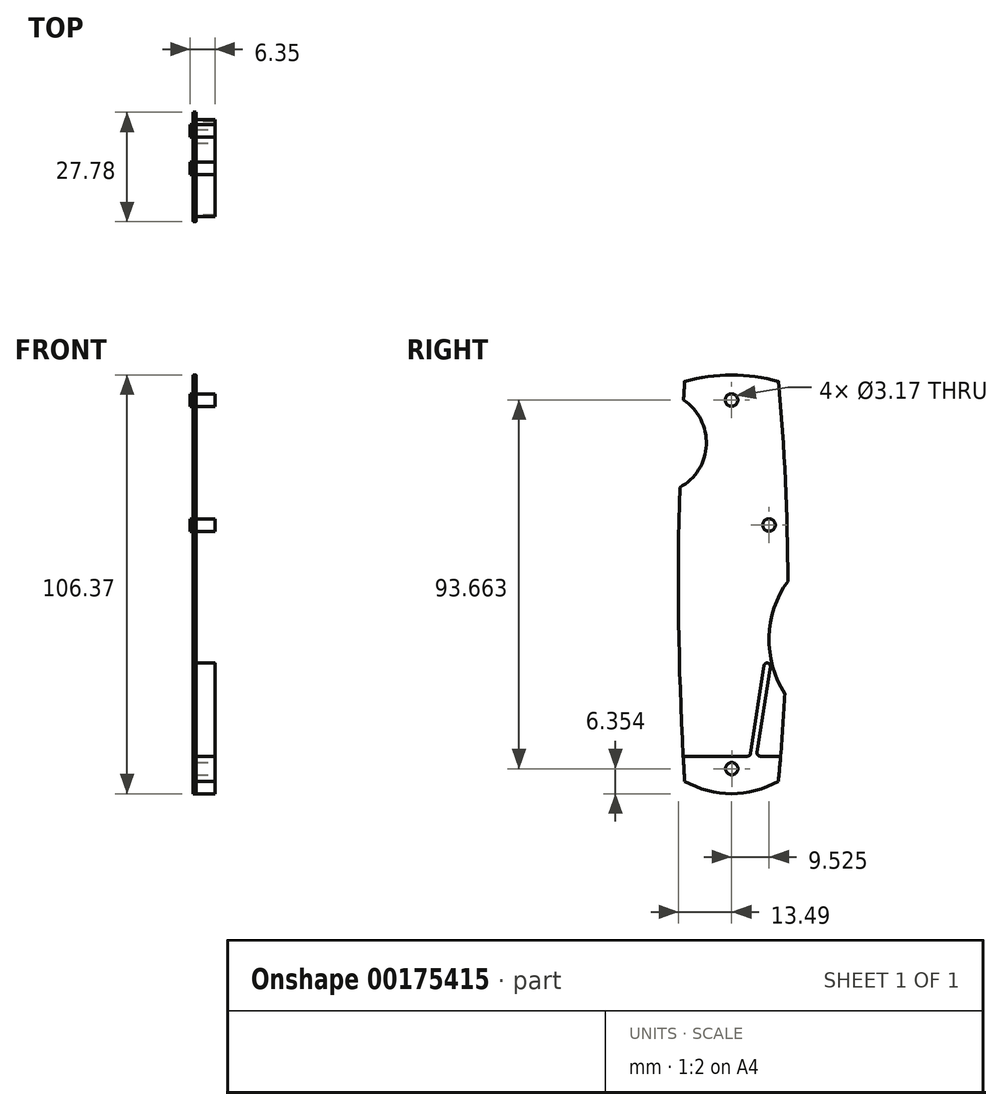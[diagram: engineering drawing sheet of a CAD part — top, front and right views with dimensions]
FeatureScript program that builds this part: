
annotation { "Feature Type Name" : "Feature", "Feature Type Description" : "" }
export const myFeature = defineFeature(function(context is Context, id is Id, definition is map)
    precondition{}
    {
        {
            var Q0;
            Q0=qCreatedBy(makeId("Right.planeOp"),FACE);
            var sketch = newSketch(context, id + "F0", { "sketchPlane" : qUnion([Q0])});
            skLineSegment(sketch, "E0", {"start": v(0, 50.8) * mm, "end": v(0, -50.8) * mm, "construction": true});
            skPoint(sketch, "E1", {"position": v(0, 46.04) * mm});
            skCircle(sketch, "E2", {"center": v(0, 46.04) * mm, "radius": 1.59 * mm});
            skLineSegment(sketch, "E3", {"start": v(-9.53, 46.04) * mm, "end": v(9.53, 46.04) * mm, "construction": true});
            skLineSegment(sketch, "E4", {"start": v(9.53, 46.04) * mm, "end": v(9.53, -17.46) * mm, "construction": true});
            skPoint(sketch, "E5", {"position": v(9.53, 14.29) * mm});
            skCircle(sketch, "E6", {"center": v(9.53, 14.29) * mm, "radius": 1.59 * mm});
            skLineSegment(sketch, "E7", {"start": v(-11.9, 50.8) * mm, "end": v(11.9, 50.8) * mm, "construction": true});
            skPoint(sketch, "E8", {"position": v(0, 14.29) * mm});
            skLineSegment(sketch, "E9", {"start": v(0, 14.29) * mm, "end": v(12.7, 14.29) * mm, "construction": true});
            skPoint(sketch, "E10", {"position": v(9.53, 0) * mm});
            skLineSegment(sketch, "E11", {"start": v(9.53, 0) * mm, "end": v(14.29, 0) * mm, "construction": true});
            skLineSegment(sketch, "E12.MirrorCS", {"start": v(0, -14.29) * mm, "end": v(12.7, -14.29) * mm, "construction": true});
            skPoint(sketch, "E13.MirrorP", {"position": v(9.53, -14.29) * mm});
            skLineSegment(sketch, "E14", {"start": v(11.9, -50.8) * mm, "end": v(-11.9, -50.8) * mm, "construction": true});
            skArc(sketch, "E15", {"start": v(11.9, -50.8) * mm, "mid": v(14.29, 0) * mm, "end": v(11.9, 50.8) * mm});
            skLineSegment(sketch, "E16.MirrorCS", {"start": v(9.53, -28.58) * mm, "end": v(14.29, -28.58) * mm, "construction": true});
            skPoint(sketch, "E17", {"position": v(13.54, -28.58) * mm});
            skArc(sketch, "E18", {"start": v(14.29, 0) * mm, "mid": v(9.53, -14.17) * mm, "end": v(13.54, -28.58) * mm});
            skLineSegment(sketch, "E19", {"start": v(0, -50.8) * mm, "end": v(0, -53.98) * mm, "construction": true});
            skArc(sketch, "E20", {"start": v(-11.9, -50.8) * mm, "mid": v(0, -53.98) * mm, "end": v(11.9, -50.8) * mm});
            skLineSegment(sketch, "E21", {"start": v(0, 50.8) * mm, "end": v(0, 52.39) * mm, "construction": true});
            skArc(sketch, "E22", {"start": v(11.9, 50.8) * mm, "mid": v(0, 52.39) * mm, "end": v(-11.9, 50.8) * mm});
            skLineSegment(sketch, "E23", {"start": v(-11.9, 50.8) * mm, "end": v(-11.9, -50.8) * mm, "construction": true});
            skLineSegment(sketch, "E24", {"start": v(-11.9, 0) * mm, "end": v(-13.5, 0) * mm, "construction": true});
            skPoint(sketch, "E24.endSnap0", {"position": v(-11.9, 0) * mm});
            skArc(sketch, "E25", {"start": v(-11.9, 50.8) * mm, "mid": v(-13.5, 0) * mm, "end": v(-11.9, -50.8) * mm});
            skPoint(sketch, "E26", {"position": v(-12.2, 46.04) * mm});
            skPoint(sketch, "E27", {"position": v(-13.14, 23.83) * mm});
            skLineSegment(sketch, "E28", {"start": v(-12.74, 34.94) * mm, "end": v(-6.4, 34.94) * mm, "construction": true});
            skArc(sketch, "E29", {"start": v(-13.14, 23.83) * mm, "mid": v(-6.4, 34.67) * mm, "end": v(-12.2, 46.04) * mm});
            skSolve(sketch);
        }
        {
            var Q0;
            Q0=makeQuery(id+"F0.imprint","IMPRINT",FACE,{"disambiguationData":[TD([[makeQuery(id+"F0.imprint","IMPRINT",EDGE,{"derivedFrom":sQuery(id+"F0.wireOp",EDGE,"E2")}),-1.0]])]});
            extrude(context, id + "F1", {"entities" : qUnion([Q0]), "oppositeDirection" : true, "depth" : 0.8 * mm});
        }
        {
            var Q0;
            Q0=makeQuery(id+"F0.imprint","IMPRINT",FACE,{"disambiguationData":[TD([[makeQuery(id+"F0.imprint","IMPRINT",EDGE,{"derivedFrom":sQuery(id+"F0.wireOp",EDGE,"E2")}),1.0]])]});
            var Q1;
            Q1=makeQuery(id+"F0.imprint","IMPRINT",FACE,{"disambiguationData":[TD([[makeQuery(id+"F0.imprint","IMPRINT",EDGE,{"derivedFrom":sQuery(id+"F0.wireOp",EDGE,"E6")}),1.0]])]});
            extrude(context, id + "F2", {"entities" : qUnion([Q0, Q1]), "depth" : 4.76 * mm, "hasSecondDirection" : true, "secondDirectionOppositeDirection" : true, "secondDirectionDepth" : 1.59 * mm});
        }
        {
            var Q0;
            Q0=makeQuery(id+"F1.opExtrude","CAP_FACE",FACE,{"disambiguationData":[OSD([sQuery(id+"F0.wireOp",EDGE,"E2"),sQuery(id+"F0.wireOp",EDGE,"E6"),sQuery(id+"F0.wireOp",EDGE,"E15"),sQuery(id+"F0.wireOp",EDGE,"E18"),sQuery(id+"F0.wireOp",EDGE,"E20"),sQuery(id+"F0.wireOp",EDGE,"E22"),sQuery(id+"F0.wireOp",EDGE,"E25")])],"isStart":true});
            var sketch = newSketch(context, id + "F6", { "sketchPlane" : qUnion([Q0])});
            skLineSegment(sketch, "E30", {"start": v(0, -53.98) * mm, "end": v(0, -44.45) * mm, "construction": true});
            skPoint(sketch, "E30.endSnap0", {"position": v(0, -53.98) * mm});
            skLineSegment(sketch, "E31", {"start": v(-12.28, -44.45) * mm, "end": v(12.47, -44.45) * mm});
            skLineSegment(sketch, "E32", {"start": v(9.94, -20.91) * mm, "end": v(6.35, -44.45) * mm});
            skLineSegment(sketch, "E33", {"start": v(9.94, -20.91) * mm, "end": v(8.38, -20.67) * mm});
            skLineSegment(sketch, "E34", {"start": v(8.38, -20.67) * mm, "end": v(4.74, -44.45) * mm});
            skSolve(sketch);
        }
        {
            var Q0;
            {var subQ0=sQuery(id+"F0.wireOp",EDGE,"E20");var subQ1=makeQuery(id+"F1.opExtrude","CAP_EDGE",EDGE,{"disambiguationData":[OSD([subQ0])],"isStart":true});Q0=makeQuery(id+"F6.imprint","IMPRINT",FACE,{"disambiguationData":[TD([[makeQuery(id+"F6.imprint","IMPRINT",EDGE,{"derivedFrom":subQ1}),1.0]])]});}
            var Q1;
            {var subQ0=sQuery(id+"F6.wireOp",EDGE,"E34");Q1=makeQuery(id+"F6.imprint","IMPRINT",FACE,{"disambiguationData":[TD([[makeQuery(id+"F6.imprint","IMPRINT",EDGE,{"derivedFrom":subQ0}),1.0]])]});}
            var Q2;
            {var subQ0=sQuery(id+"F6.wireOp",EDGE,"E33");var subQ1=sQuery(id+"F6.wireOp",EDGE,"E32");var subQ2=makeQuery(id+"F6.imprint","INTERSECT",VERTEX,{"derivedFrom":[subQ1,subQ0]});Q2=makeQuery(id+"F6.imprint","IMPRINT",FACE,{"disambiguationData":[TD([[makeQuery(id+"F6.imprint","IMPRINT",EDGE,{"disambiguationData":[TD([[subQ2,-1.0]])],"derivedFrom":subQ1}),-1.0]])]});}
            extrude(context, id + "F3", {"entities" : qUnion([Q0, Q1, Q2]), "depth" : 4.76 * mm});
        }
        {
            var Q0;
            Q0=makeQuery(id+"F3.opExtrude","SWEPT_EDGE",EDGE,{"disambiguationData":[OSD([sQuery(id+"F6.wireOp",EDGE,"E31"),sQuery(id+"F6.wireOp",EDGE,"E34")])]});
            var Q1;
            Q1=makeQuery(id+"F3.opExtrude","SWEPT_EDGE",EDGE,{"disambiguationData":[OSD([sQuery(id+"F6.wireOp",EDGE,"E31"),sQuery(id+"F6.wireOp",EDGE,"E32")])]});
            var Q2;
            Q2=makeQuery(id+"F3.opExtrude","SWEPT_EDGE",EDGE,{"disambiguationData":[OSD([sQuery(id+"F6.wireOp",EDGE,"E32"),sQuery(id+"F6.wireOp",EDGE,"E33")])]});
            var Q3;
            Q3=makeQuery(id+"F3.opExtrude","SWEPT_EDGE",EDGE,{"disambiguationData":[OSD([sQuery(id+"F6.wireOp",EDGE,"E33"),sQuery(id+"F6.wireOp",EDGE,"E34")])]});
            fillet(context, id + "F4", {"entities" : qUnion([Q0, Q1, Q2, Q3]), "radius" : 0.8 * mm, "tangentPropagation" : true, "allowEdgeOverflow" : false});
        }
        {
            var Q0;
            Q0=makeQuery(id+"F3.opExtrude","CAP_FACE",FACE,{"disambiguationData":[OSD([sQuery(id+"F0.wireOp",EDGE,"E15"),sQuery(id+"F0.wireOp",EDGE,"E20"),sQuery(id+"F0.wireOp",EDGE,"E25"),sQuery(id+"F6.wireOp",EDGE,"E31"),sQuery(id+"F6.wireOp",EDGE,"E32"),sQuery(id+"F6.wireOp",EDGE,"E33"),sQuery(id+"F6.wireOp",EDGE,"E34")])],"isStart":false});
            var sketch = newSketch(context, id + "F5", { "sketchPlane" : qUnion([Q0])});
            skLineSegment(sketch, "E35", {"start": v(-12.1, -47.63) * mm, "end": v(12.2, -47.63) * mm});
            skPoint(sketch, "E35.startSnap0", {"position": v(12.2, -47.63) * mm});
            skPoint(sketch, "E35.endSnap0", {"position": v(12.2, -47.63) * mm});
            skPoint(sketch, "E35.endSnap1", {"position": v(-12.1, -47.63) * mm});
            skPoint(sketch, "E36", {"position": v(0.05, -47.63) * mm});
            skSolve(sketch);
        }
        {
            var Q0;
            Q0=sQuery(id+"F5.wireOp",VERTEX,"E36");
            var Q1;
            Q1=makeQuery(id+"F3.opExtrude","SWEPT_BODY",BODY,{"disambiguationData":[OSD([sQuery(id+"F0.wireOp",EDGE,"E15"),sQuery(id+"F0.wireOp",EDGE,"E20"),sQuery(id+"F0.wireOp",EDGE,"E25"),sQuery(id+"F6.wireOp",EDGE,"E31"),sQuery(id+"F6.wireOp",EDGE,"E32"),sQuery(id+"F6.wireOp",EDGE,"E33"),sQuery(id+"F6.wireOp",EDGE,"E34")])]});
            var Q2;
            Q2=makeQuery(id+"F1.opExtrude","SWEPT_BODY",BODY,{"disambiguationData":[OSD([sQuery(id+"F0.wireOp",EDGE,"E2"),sQuery(id+"F0.wireOp",EDGE,"E6"),sQuery(id+"F0.wireOp",EDGE,"E15"),sQuery(id+"F0.wireOp",EDGE,"E18"),sQuery(id+"F0.wireOp",EDGE,"E20"),sQuery(id+"F0.wireOp",EDGE,"E22"),sQuery(id+"F0.wireOp",EDGE,"E25")])]});
            hole(context, id + "F7", {"style" : HoleStyle.SIMPLE, "endStyle" : HoleEndStyle.THROUGH, "holeDiameter" : 3.17 * mm, "locations" : qUnion([Q0]), "scope" : qUnion([Q1, Q2]), "isTappedThrough" : true});
        }
    });
